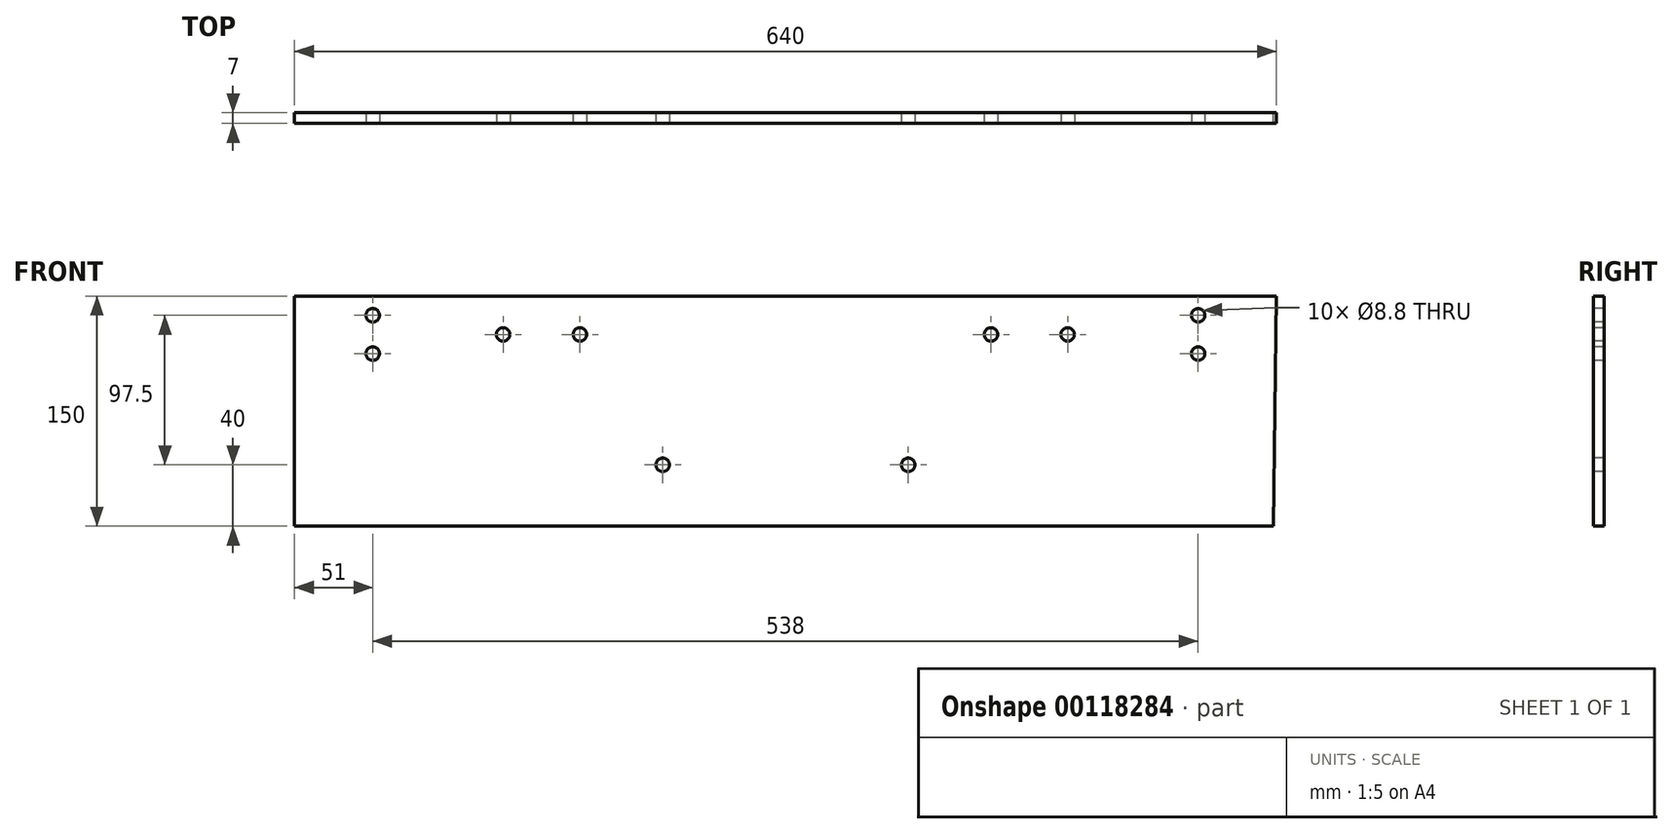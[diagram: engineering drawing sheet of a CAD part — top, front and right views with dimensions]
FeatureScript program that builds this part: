
annotation { "Feature Type Name" : "Feature", "Feature Type Description" : "" }
export const myFeature = defineFeature(function(context is Context, id is Id, definition is map)
    precondition{}
    {
        {
            var Q0;
            Q0=qCreatedBy(makeId("Front.planeOp"),FACE);
            var sketch = newSketch(context, id + "F0", { "sketchPlane" : qUnion([Q0])});
            skLineSegment(sketch, "E0.top", {"start": v(319, -450) * mm, "end": v(-319, -450) * mm});
            skPoint(sketch, "E0.middle", {"position": v(0, 0) * mm});
            skLineSegment(sketch, "E1", {"start": v(-319, -450) * mm, "end": v(-319, -300) * mm});
            skLineSegment(sketch, "E2", {"start": v(-319, -300) * mm, "end": v(321, -300) * mm});
            skLineSegment(sketch, "E3", {"start": v(321, -300) * mm, "end": v(319, -450) * mm});
            skLineSegment(sketch, "E4", {"start": v(-319, -300) * mm, "end": v(-308, -300) * mm});
            skLineSegment(sketch, "E5", {"start": v(-308, -300) * mm, "end": v(-308, -450) * mm});
            skLineSegment(sketch, "E6", {"start": v(321, -300) * mm, "end": v(310, -300) * mm});
            skLineSegment(sketch, "E7", {"start": v(310, -300) * mm, "end": v(310, -450) * mm});
            skSolve(sketch);
        }
        {
            var Q0;
            Q0=makeQuery(id+"F0.imprint","IMPRINT",FACE,{"disambiguationData":[TD([[makeQuery(id+"F0.imprint","IMPRINT",EDGE,{"derivedFrom":sQuery(id+"F0.wireOp",EDGE,"E2")}),-1.0]])]});
            extrude(context, id + "F1", {"entities" : qUnion([Q0]), "depth" : 7 * mm});
        }
        {
            var Q0;
            Q0=makeQuery(id+"F1.opExtrude","CAP_FACE",FACE,{"disambiguationData":[OSD([sQuery(id+"F0.wireOp",EDGE,"E0.top"),sQuery(id+"F0.wireOp",EDGE,"E2"),sQuery(id+"F0.wireOp",EDGE,"E5"),sQuery(id+"F0.wireOp",EDGE,"E7")])],"isStart":false});
            var sketch = newSketch(context, id + "F2", { "sketchPlane" : qUnion([Q0])});
            skLineSegment(sketch, "E8", {"start": v(-308, -300) * mm, "end": v(-158, -300) * mm});
            skLineSegment(sketch, "E9", {"start": v(310, -300) * mm, "end": v(160, -300) * mm});
            skLineSegment(sketch, "E10", {"start": v(160, -300) * mm, "end": v(-158, -300) * mm});
            skLineSegment(sketch, "E11.MirrorCS", {"start": v(198, -300) * mm, "end": v(-208, -300) * mm});
            skLineSegment(sketch, "E12.MirrorCS", {"start": v(-308, -300) * mm, "end": v(-208, -300) * mm});
            skLineSegment(sketch, "E13", {"start": v(-158, -300) * mm, "end": v(-158, -450) * mm});
            skLineSegment(sketch, "E14", {"start": v(-158, -450) * mm, "end": v(-208, -450) * mm});
            skLineSegment(sketch, "E15", {"start": v(-158, -450) * mm, "end": v(-128, -450) * mm});
            skLineSegment(sketch, "E16.bottom", {"start": v(-208, -450) * mm, "end": v(-108, -450) * mm});
            skLineSegment(sketch, "E16.top", {"start": v(-208, -400) * mm, "end": v(-108, -400) * mm});
            skLineSegment(sketch, "E16.left", {"start": v(-208, -450) * mm, "end": v(-208, -400) * mm});
            skLineSegment(sketch, "E16.right", {"start": v(-108, -450) * mm, "end": v(-108, -400) * mm});
            skLineSegment(sketch, "E17", {"start": v(-158, -450) * mm, "end": v(-108, -400) * mm});
            skLineSegment(sketch, "E18", {"start": v(-158, -300) * mm, "end": v(-158, -350) * mm});
            skLineSegment(sketch, "E19", {"start": v(-158, -350) * mm, "end": v(-208, -350) * mm});
            skLineSegment(sketch, "E20", {"start": v(-208, -350) * mm, "end": v(-158, -300) * mm});
            skLineSegment(sketch, "E21", {"start": v(-158, -300) * mm, "end": v(-108, -300) * mm});
            skLineSegment(sketch, "E22", {"start": v(-108, -300) * mm, "end": v(-108, -350) * mm});
            skLineSegment(sketch, "E23", {"start": v(-208, -350) * mm, "end": v(-208, -300) * mm});
            skLineSegment(sketch, "E24", {"start": v(-108, -350) * mm, "end": v(-158, -350) * mm});
            skLineSegment(sketch, "E25", {"start": v(-158, -350) * mm, "end": v(-108, -300) * mm});
            skLineSegment(sketch, "E26", {"start": v(-208, -450) * mm, "end": v(-158, -400) * mm});
            skLineSegment(sketch, "E27", {"start": v(160, -300) * mm, "end": v(160, -450) * mm});
            skLineSegment(sketch, "E28", {"start": v(160, -450) * mm, "end": v(160, -400) * mm});
            skLineSegment(sketch, "E29", {"start": v(160, -400) * mm, "end": v(210, -400) * mm});
            skLineSegment(sketch, "E30", {"start": v(210, -400) * mm, "end": v(210, -450) * mm});
            skLineSegment(sketch, "E31", {"start": v(160, -450) * mm, "end": v(210, -400) * mm});
            skLineSegment(sketch, "E32", {"start": v(160, -400) * mm, "end": v(110, -400) * mm});
            skLineSegment(sketch, "E33", {"start": v(110, -400) * mm, "end": v(110, -450) * mm});
            skLineSegment(sketch, "E34", {"start": v(110, -450) * mm, "end": v(160, -400) * mm});
            skLineSegment(sketch, "E35", {"start": v(160, -300) * mm, "end": v(160, -350) * mm});
            skLineSegment(sketch, "E36", {"start": v(160, -350) * mm, "end": v(160, -350) * mm});
            skLineSegment(sketch, "E37", {"start": v(160, -350) * mm, "end": v(160, -300) * mm});
            skLineSegment(sketch, "E38", {"start": v(160, -300) * mm, "end": v(210, -300) * mm});
            skLineSegment(sketch, "E39", {"start": v(210, -300) * mm, "end": v(210, -350) * mm});
            skLineSegment(sketch, "E40", {"start": v(210, -350) * mm, "end": v(160, -350) * mm});
            skLineSegment(sketch, "E41", {"start": v(210, -300) * mm, "end": v(160, -350) * mm});
            skLineSegment(sketch, "E42", {"start": v(160, -450) * mm, "end": v(135, -425) * mm});
            skLineSegment(sketch, "E43", {"start": v(-158, -450) * mm, "end": v(-183, -425) * mm});
            skLineSegment(sketch, "E44", {"start": v(-158, -350) * mm, "end": v(-183, -325) * mm});
            skLineSegment(sketch, "E45", {"start": v(160, -350) * mm, "end": v(160, -325) * mm});
            skLineSegment(sketch, "E46", {"start": v(210, -350) * mm, "end": v(185, -325) * mm});
            skLineSegment(sketch, "E47", {"start": v(210, -450) * mm, "end": v(185, -425) * mm});
            skLineSegment(sketch, "E48", {"start": v(-108, -450) * mm, "end": v(-133, -425) * mm});
            skLineSegment(sketch, "E49", {"start": v(-108, -350) * mm, "end": v(-133, -325) * mm});
            skLineSegment(sketch, "E50", {"start": v(160, -300) * mm, "end": v(110, -300) * mm});
            skLineSegment(sketch, "E51", {"start": v(160, -350) * mm, "end": v(110, -350) * mm});
            skLineSegment(sketch, "E52", {"start": v(110, -350) * mm, "end": v(110, -300) * mm});
            skLineSegment(sketch, "E53", {"start": v(160, -350) * mm, "end": v(110, -300) * mm});
            skLineSegment(sketch, "E54", {"start": v(135, -325) * mm, "end": v(160, -300) * mm});
            skLineSegment(sketch, "E55.0.0", {"start": v(-308, -450) * mm, "end": v(310, -450) * mm});
            skLineSegment(sketch, "E55.0.1", {"start": v(310, -450) * mm, "end": v(310, -300) * mm});
            skLineSegment(sketch, "E55.0.2", {"start": v(310, -300) * mm, "end": v(-308, -300) * mm});
            skLineSegment(sketch, "E55.0.3", {"start": v(-308, -300) * mm, "end": v(-308, -450) * mm});
            skSolve(sketch);
        }
        {
            var Q0;
            Q0=sQuery(id+"F2.wireOp",VERTEX,"E44.end");
            var Q1;
            Q1=sQuery(id+"F2.wireOp",VERTEX,"E49.end");
            var Q2;
            Q2=sQuery(id+"F2.wireOp",VERTEX,"E46.end");
            var Q3;
            Q3=sQuery(id+"F2.wireOp",VERTEX,"IJQfvNGp-jPv3-fynY-866w-Etbx68AJoQDy.end");
            var Q4;
            Q4=sQuery(id+"F2.wireOp",VERTEX,"E54.start");
            var Q5;
            Q5=makeQuery(id+"F1.opExtrude","SWEPT_BODY",BODY,{"disambiguationData":[OSD([sQuery(id+"F0.wireOp",EDGE,"E0.top"),sQuery(id+"F0.wireOp",EDGE,"E2"),sQuery(id+"F0.wireOp",EDGE,"E5"),sQuery(id+"F0.wireOp",EDGE,"E7")])]});
            hole(context, id + "F3", {"style" : HoleStyle.SIMPLE, "endStyle" : HoleEndStyle.THROUGH, "standardTappedOrClearance" : lookupTablePath({ "standard" : "ISO", "fit" : "Normal", "size" : "M8", "type" : "Clearance" }), "standardBlindInLast" : lookupTablePath({ "fit" : "Standard", "standard" : "ISO", "size" : "M8", "type" : "Clearance" }), "holeDiameter" : 8.8 * mm, "locations" : qUnion([Q0, Q1, Q2, Q3, Q4]), "scope" : qUnion([Q5]), "isTappedThrough" : true});
        }
        {
            var Q0;
            Q0=makeQuery(id+"F1.opExtrude","CAP_FACE",FACE,{"disambiguationData":[OSD([sQuery(id+"F0.wireOp",EDGE,"E0.top"),sQuery(id+"F0.wireOp",EDGE,"E2"),sQuery(id+"F0.wireOp",EDGE,"E5"),sQuery(id+"F0.wireOp",EDGE,"E7")])],"isStart":false});
            var sketch = newSketch(context, id + "F4", { "sketchPlane" : qUnion([Q0])});
            skLineSegment(sketch, "E56", {"start": v(-183, -325) * mm, "end": v(-133, -325) * mm});
            skLineSegment(sketch, "E57", {"start": v(-133, -325) * mm, "end": v(-133, -300) * mm});
            skLineSegment(sketch, "E58", {"start": v(-183, -325) * mm, "end": v(-183, -300) * mm});
            skLineSegment(sketch, "E59", {"start": v(-308, -300) * mm, "end": v(-308, -350) * mm});
            skLineSegment(sketch, "E60", {"start": v(-308, -350) * mm, "end": v(-238, -350) * mm});
            skLineSegment(sketch, "E61", {"start": v(-238, -350) * mm, "end": v(-238, -300) * mm});
            skLineSegment(sketch, "E62", {"start": v(-238, -300) * mm, "end": v(-308, -300) * mm});
            skLineSegment(sketch, "E63", {"start": v(-308, -300) * mm, "end": v(-298, -300) * mm});
            skLineSegment(sketch, "E64", {"start": v(-298, -300) * mm, "end": v(-298, -350) * mm});
            skLineSegment(sketch, "E65", {"start": v(-298, -325) * mm, "end": v(-238, -350) * mm});
            skLineSegment(sketch, "E66", {"start": v(-298, -325) * mm, "end": v(-238, -300) * mm});
            skLineSegment(sketch, "E67", {"start": v(-268, -312.5) * mm, "end": v(-268, -337.5) * mm});
            skLineSegment(sketch, "E68", {"start": v(310, -300) * mm, "end": v(310, -350) * mm});
            skLineSegment(sketch, "E69", {"start": v(310, -350) * mm, "end": v(240, -350) * mm});
            skLineSegment(sketch, "E70", {"start": v(240, -350) * mm, "end": v(240, -300) * mm});
            skLineSegment(sketch, "E71", {"start": v(240, -300) * mm, "end": v(310, -300) * mm});
            skLineSegment(sketch, "E72", {"start": v(310, -300) * mm, "end": v(300, -300) * mm});
            skLineSegment(sketch, "E73", {"start": v(300, -300) * mm, "end": v(300, -350) * mm});
            skLineSegment(sketch, "E74", {"start": v(300, -325) * mm, "end": v(240, -350) * mm});
            skLineSegment(sketch, "E75", {"start": v(240, -300) * mm, "end": v(300, -325) * mm});
            skLineSegment(sketch, "E76", {"start": v(270, -337.5) * mm, "end": v(270, -312.5) * mm});
            skLineSegment(sketch, "E77", {"start": v(-308, -410) * mm, "end": v(310, -410) * mm});
            skLineSegment(sketch, "E78", {"start": v(1, -410) * mm, "end": v(-79, -410) * mm});
            skLineSegment(sketch, "E79", {"start": v(1, -410) * mm, "end": v(81, -410) * mm});
            skLineSegment(sketch, "E80", {"start": v(-268, -337.5) * mm, "end": v(-308, -337.5) * mm});
            skLineSegment(sketch, "E81", {"start": v(-308, -450) * mm, "end": v(310, -450) * mm});
            skSolve(sketch);
        }
        {
            var Q0;
            Q0=sQuery(id+"F4.wireOp",VERTEX,"E67.end");
            var Q1;
            Q1=sQuery(id+"F4.wireOp",VERTEX,"E67.start");
            var Q2;
            Q2=sQuery(id+"F4.wireOp",VERTEX,"E76.start");
            var Q3;
            Q3=sQuery(id+"F4.wireOp",VERTEX,"E76.end");
            var Q4;
            Q4=sQuery(id+"F4.wireOp",VERTEX,"E78.end");
            var Q5;
            Q5=sQuery(id+"F4.wireOp",VERTEX,"E79.end");
            var Q6;
            Q6=makeQuery(id+"F1.opExtrude","SWEPT_BODY",BODY,{"disambiguationData":[OSD([sQuery(id+"F0.wireOp",EDGE,"E0.top"),sQuery(id+"F0.wireOp",EDGE,"E2"),sQuery(id+"F0.wireOp",EDGE,"E5"),sQuery(id+"F0.wireOp",EDGE,"E7")])]});
            hole(context, id + "F5", {"style" : HoleStyle.SIMPLE, "endStyle" : HoleEndStyle.THROUGH, "standardTappedOrClearance" : lookupTablePath({ "standard" : "ISO", "fit" : "Normal", "size" : "M8", "type" : "Clearance" }), "standardBlindInLast" : lookupTablePath({ "fit" : "Standard", "standard" : "ISO", "size" : "M8", "type" : "Clearance" }), "holeDiameter" : 8.8 * mm, "locations" : qUnion([Q0, Q1, Q2, Q3, Q4, Q5]), "scope" : qUnion([Q6]), "isTappedThrough" : true});
        }
    });
